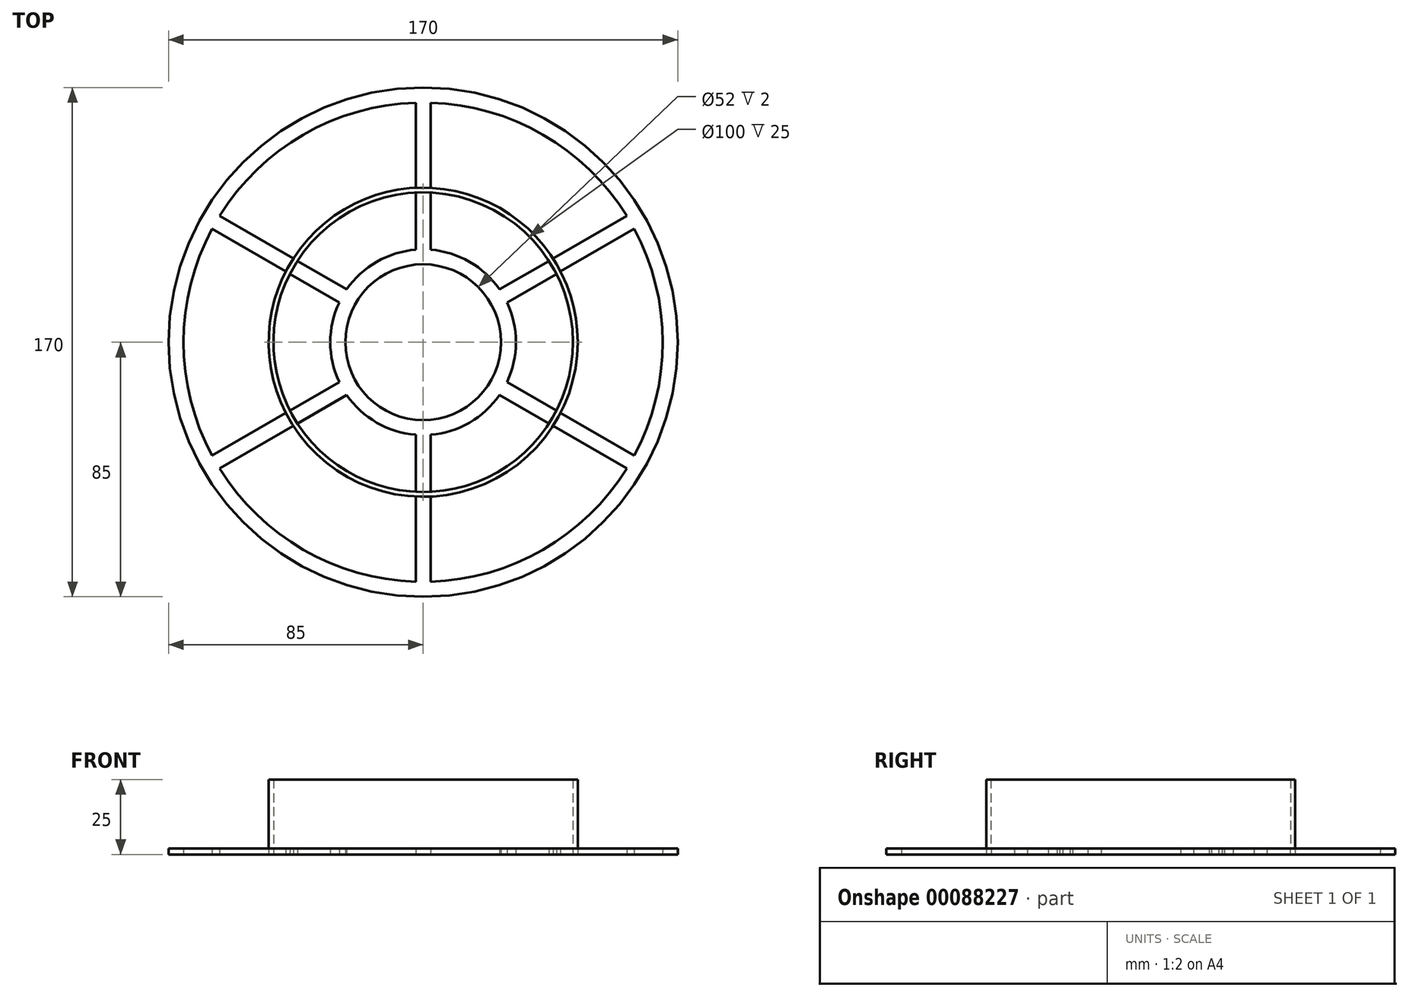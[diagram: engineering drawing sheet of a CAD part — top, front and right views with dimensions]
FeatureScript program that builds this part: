
annotation { "Feature Type Name" : "Feature", "Feature Type Description" : "" }
export const myFeature = defineFeature(function(context is Context, id is Id, definition is map)
    precondition{}
    {
        {
            var Q0;
            Q0=qCreatedBy(makeId("Top.planeOp"),FACE);
            var sketch = newSketch(context, id + "F0", { "sketchPlane" : qUnion([Q0])});
            skCircle(sketch, "E0", {"center": v(0, 0) * mm, "radius": 26 * mm});
            skCircle(sketch, "E1", {"center": v(0, 0) * mm, "radius": 50 * mm});
            skCircle(sketch, "E2.0", {"center": v(0, 0) * mm, "radius": 51.6 * mm});
            skCircle(sketch, "E3", {"center": v(0, 0) * mm, "radius": 85 * mm});
            skArc(sketch, "E4.0", {"start": v(-2.5, 79.96) * mm, "mid": v(-40, 69.28) * mm, "end": v(-68, 42.15) * mm});
            skLineSegment(sketch, "E5.0", {"start": v(2.5, 30.9) * mm, "end": v(2.5, 49.94) * mm});
            skLineSegment(sketch, "E6.0", {"start": v(-2.5, 30.9) * mm, "end": v(-2.5, 49.94) * mm});
            skLineSegment(sketch, "E7.trimOffspring", {"start": v(-2.5, 51.54) * mm, "end": v(-2.5, 79.96) * mm});
            skLineSegment(sketch, "E8.trimOffspring", {"start": v(2.5, 51.54) * mm, "end": v(2.5, 79.96) * mm});
            skArc(sketch, "E9.0", {"start": v(-2.5, 30.9) * mm, "mid": v(-15.5, 26.85) * mm, "end": v(-25.5, 17.61) * mm});
            skLineSegment(sketch, "E10.1.0", {"start": v(-45.88, 23.6) * mm, "end": v(-70.5, 37.82) * mm});
            skLineSegment(sketch, "E10.1.1", {"start": v(-43.38, 27.93) * mm, "end": v(-68, 42.15) * mm});
            skLineSegment(sketch, "E10.1.2", {"start": v(-25.5, 17.61) * mm, "end": v(-42, 27.13) * mm});
            skLineSegment(sketch, "E10.1.3", {"start": v(-28, 13.28) * mm, "end": v(-44.5, 22.8) * mm});
            skLineSegment(sketch, "E10.2.0", {"start": v(-43.38, -27.93) * mm, "end": v(-68, -42.15) * mm});
            skLineSegment(sketch, "E10.2.1", {"start": v(-45.88, -23.6) * mm, "end": v(-70.5, -37.82) * mm});
            skLineSegment(sketch, "E10.2.2", {"start": v(-28, -13.28) * mm, "end": v(-44.5, -22.8) * mm});
            skLineSegment(sketch, "E10.2.3", {"start": v(-25.5, -17.61) * mm, "end": v(-42, -27.13) * mm});
            skLineSegment(sketch, "E11.1.3.0", {"start": v(2.5, -51.54) * mm, "end": v(2.5, -79.96) * mm});
            skLineSegment(sketch, "E11.3.3.0", {"start": v(-2.5, -51.54) * mm, "end": v(-2.5, -79.96) * mm});
            skLineSegment(sketch, "E11.6.3.0", {"start": v(-2.5, -30.9) * mm, "end": v(-2.5, -49.94) * mm});
            skLineSegment(sketch, "E11.9.3.0", {"start": v(2.5, -30.9) * mm, "end": v(2.5, -49.94) * mm});
            skLineSegment(sketch, "E11.1.4.0", {"start": v(45.88, -23.6) * mm, "end": v(70.5, -37.82) * mm});
            skLineSegment(sketch, "E11.3.4.0", {"start": v(43.38, -27.93) * mm, "end": v(68, -42.15) * mm});
            skLineSegment(sketch, "E11.6.4.0", {"start": v(25.5, -17.61) * mm, "end": v(42, -27.13) * mm});
            skLineSegment(sketch, "E11.9.4.0", {"start": v(28, -13.28) * mm, "end": v(44.5, -22.8) * mm});
            skLineSegment(sketch, "E11.1.5.0", {"start": v(43.38, 27.93) * mm, "end": v(68, 42.15) * mm});
            skLineSegment(sketch, "E11.3.5.0", {"start": v(45.88, 23.6) * mm, "end": v(70.5, 37.82) * mm});
            skLineSegment(sketch, "E11.6.5.0", {"start": v(28, 13.28) * mm, "end": v(44.5, 22.8) * mm});
            skLineSegment(sketch, "E11.9.5.0", {"start": v(25.5, 17.61) * mm, "end": v(42, 27.13) * mm});
            skArc(sketch, "E12.trimOffspring", {"start": v(-28, 13.28) * mm, "mid": v(-31, 0) * mm, "end": v(-28, -13.28) * mm});
            skArc(sketch, "E13.trimOffspring", {"start": v(25.5, 17.61) * mm, "mid": v(15.5, 26.85) * mm, "end": v(2.5, 30.9) * mm});
            skArc(sketch, "E14.trimOffspring", {"start": v(28, -13.28) * mm, "mid": v(31, 0) * mm, "end": v(28, 13.28) * mm});
            skArc(sketch, "E15.trimOffspring", {"start": v(2.5, -30.9) * mm, "mid": v(15.5, -26.85) * mm, "end": v(25.5, -17.61) * mm});
            skArc(sketch, "E16.trimOffspring", {"start": v(-25.5, -17.61) * mm, "mid": v(-15.5, -26.85) * mm, "end": v(-2.5, -30.9) * mm});
            skArc(sketch, "E17.trimOffspring", {"start": v(70.5, -37.82) * mm, "mid": v(80, 0) * mm, "end": v(70.5, 37.82) * mm});
            skArc(sketch, "E18.trimOffspring", {"start": v(68, 42.15) * mm, "mid": v(40, 69.28) * mm, "end": v(2.5, 79.96) * mm});
            skArc(sketch, "E19.trimOffspring", {"start": v(2.5, -79.96) * mm, "mid": v(40, -69.28) * mm, "end": v(68, -42.15) * mm});
            skArc(sketch, "E20.trimOffspring", {"start": v(-68, -42.15) * mm, "mid": v(-40, -69.28) * mm, "end": v(-2.5, -79.96) * mm});
            skArc(sketch, "E21.trimOffspring", {"start": v(-70.5, 37.82) * mm, "mid": v(-80, 0) * mm, "end": v(-70.5, -37.82) * mm});
            skSolve(sketch);
        }
        {
            var Q0;
            Q0=makeQuery(id+"F0.imprint","IMPRINT",FACE,{"disambiguationData":[TD([[makeQuery(id+"F0.imprint","IMPRINT",EDGE,{"derivedFrom":sQuery(id+"F0.wireOp",EDGE,"E3")}),1.0]])]});
            var Q1;
            Q1=makeQuery(id+"F0.imprint","IMPRINT",FACE,{"disambiguationData":[TD([[makeQuery(id+"F0.imprint","IMPRINT",EDGE,{"derivedFrom":sQuery(id+"F0.wireOp",EDGE,"E0")}),-1.0]])]});
            extrude(context, id + "F1", {"entities" : qUnion([Q0, Q1]), "depth" : 2 * mm});
        }
        {
            var Q0;
            {var subQ8=sQuery(id+"F0.wireOp",EDGE,"E1");var subQ10=makeQuery(id+"F0.imprint","INTERSECT",VERTEX,{"derivedFrom":[subQ8,sQuery(id+"F0.wireOp",EDGE,"E11.6.5.0")]});Q0=makeQuery(id+"F0.imprint","IMPRINT",FACE,{"disambiguationData":[TD([[makeQuery(id+"F0.imprint","IMPRINT",EDGE,{"disambiguationData":[TD([[subQ10,-1.0]])],"derivedFrom":subQ8}),-1.0]])]});}
            extrude(context, id + "F2", {"entities" : qUnion([Q0]), "operationType" : NewBodyOperationType.ADD, "depth" : 25 * mm});
        }
    });
